annotation { "Feature Type Name" : "Feature", "Feature Type Description" : "" }
export const myFeature = defineFeature(function(context is Context, id is Id, definition is map)
    precondition{}
    {
        {
            var Q0;
            Q0=qCreatedBy(makeId("Front.planeOp"),FACE);
            var sketch = newSketch(context, id + "F0", { "sketchPlane" : qUnion([Q0])});
            skLineSegment(sketch, "E0.bottom", {"start": v(-339.73, -6.1) * mm, "end": v(339.73, -6.1) * mm});
            skLineSegment(sketch, "E0.top", {"start": v(-339.73, -31.5) * mm, "end": v(339.73, -31.5) * mm});
            skLineSegment(sketch, "E0.left", {"start": v(-339.73, -6.1) * mm, "end": v(-339.73, -31.5) * mm});
            skLineSegment(sketch, "E0.right", {"start": v(339.73, -6.1) * mm, "end": v(339.73, -31.5) * mm});
            skPoint(sketch, "E1", {"position": v(0, -6.1) * mm});
            skPoint(sketch, "E2", {"position": v(0, -31.5) * mm});
            skSolve(sketch);
        }
        {
            var Q0;
            Q0=makeQuery(id+"F0.imprint","IMPRINT",FACE,{"disambiguationData":[TD([[makeQuery(id+"F0.imprint","IMPRINT",EDGE,{"derivedFrom":sQuery(id+"F0.wireOp",EDGE,"E0.bottom")}),-1.0]])]});
            extrude(context, id + "F1", {"entities" : qUnion([Q0]), "depth" : 12.7 * mm, "offsetDistance" : 25.4 * mm});
        }
        {
            var Q0;
            Q0=makeQuery(id+"Fdx1QHjnCxCHuVW_1.boolean.opBoolean","MERGE",FACE,{"derivedFrom":[makeQuery(id+"F1.opExtrude","CAP_FACE",FACE,{"disambiguationData":[OSD([sQuery(id+"F0.wireOp",EDGE,"E0.bottom"),sQuery(id+"F0.wireOp",EDGE,"E0.top"),sQuery(id+"F0.wireOp",EDGE,"E0.left"),sQuery(id+"F0.wireOp",EDGE,"E0.right")])],"isStart":false}),makeQuery(id+"Fdx1QHjnCxCHuVW_1.opExtrude","CAP_FACE",FACE,{"disambiguationData":[OSD([sQuery(id+"FkjEasT6BlErXXm_1.wireOp",EDGE,"e268084d-6bfb-4e87-9f2a-011bc5352065.sketch_text.stroke-0"),sQuery(id+"FkjEasT6BlErXXm_1.wireOp",EDGE,"e268084d-6bfb-4e87-9f2a-011bc5352065.sketch_text.stroke-1"),sQuery(id+"FkjEasT6BlErXXm_1.wireOp",EDGE,"e268084d-6bfb-4e87-9f2a-011bc5352065.sketch_text.stroke-2"),sQuery(id+"FkjEasT6BlErXXm_1.wireOp",EDGE,"e268084d-6bfb-4e87-9f2a-011bc5352065.sketch_text.stroke-3")])],"isStart":true}),makeQuery(id+"Fdx1QHjnCxCHuVW_1.opExtrude","CAP_FACE",FACE,{"disambiguationData":[OSD([sQuery(id+"FkjEasT6BlErXXm_1.wireOp",EDGE,"e268084d-6bfb-4e87-9f2a-011bc5352065.sketch_text.stroke-4"),sQuery(id+"FkjEasT6BlErXXm_1.wireOp",EDGE,"e268084d-6bfb-4e87-9f2a-011bc5352065.sketch_text.stroke-5"),sQuery(id+"FkjEasT6BlErXXm_1.wireOp",EDGE,"e268084d-6bfb-4e87-9f2a-011bc5352065.sketch_text.stroke-6"),sQuery(id+"FkjEasT6BlErXXm_1.wireOp",EDGE,"e268084d-6bfb-4e87-9f2a-011bc5352065.sketch_text.stroke-7"),sQuery(id+"FkjEasT6BlErXXm_1.wireOp",EDGE,"e268084d-6bfb-4e87-9f2a-011bc5352065.sketch_text.stroke-8"),sQuery(id+"FkjEasT6BlErXXm_1.wireOp",EDGE,"e268084d-6bfb-4e87-9f2a-011bc5352065.sketch_text.stroke-9"),sQuery(id+"FkjEasT6BlErXXm_1.wireOp",EDGE,"e268084d-6bfb-4e87-9f2a-011bc5352065.sketch_text.stroke-10"),sQuery(id+"FkjEasT6BlErXXm_1.wireOp",EDGE,"e268084d-6bfb-4e87-9f2a-011bc5352065.sketch_text.stroke-11"),sQuery(id+"FkjEasT6BlErXXm_1.wireOp",EDGE,"e268084d-6bfb-4e87-9f2a-011bc5352065.sketch_text.stroke-12"),sQuery(id+"FkjEasT6BlErXXm_1.wireOp",EDGE,"e268084d-6bfb-4e87-9f2a-011bc5352065.sketch_text.stroke-13"),sQuery(id+"FkjEasT6BlErXXm_1.wireOp",EDGE,"e268084d-6bfb-4e87-9f2a-011bc5352065.sketch_text.stroke-14"),sQuery(id+"FkjEasT6BlErXXm_1.wireOp",EDGE,"e268084d-6bfb-4e87-9f2a-011bc5352065.sketch_text.stroke-15"),sQuery(id+"FkjEasT6BlErXXm_1.wireOp",EDGE,"e268084d-6bfb-4e87-9f2a-011bc5352065.sketch_text.stroke-16"),sQuery(id+"FkjEasT6BlErXXm_1.wireOp",EDGE,"e268084d-6bfb-4e87-9f2a-011bc5352065.sketch_text.stroke-17"),sQuery(id+"FkjEasT6BlErXXm_1.wireOp",EDGE,"e268084d-6bfb-4e87-9f2a-011bc5352065.sketch_text.stroke-18"),sQuery(id+"FkjEasT6BlErXXm_1.wireOp",EDGE,"e268084d-6bfb-4e87-9f2a-011bc5352065.sketch_text.stroke-19"),sQuery(id+"FkjEasT6BlErXXm_1.wireOp",EDGE,"e268084d-6bfb-4e87-9f2a-011bc5352065.sketch_text.stroke-20"),sQuery(id+"FkjEasT6BlErXXm_1.wireOp",EDGE,"e268084d-6bfb-4e87-9f2a-011bc5352065.sketch_text.stroke-21"),sQuery(id+"FkjEasT6BlErXXm_1.wireOp",EDGE,"e268084d-6bfb-4e87-9f2a-011bc5352065.sketch_text.stroke-22"),sQuery(id+"FkjEasT6BlErXXm_1.wireOp",EDGE,"e268084d-6bfb-4e87-9f2a-011bc5352065.sketch_text.stroke-23"),sQuery(id+"FkjEasT6BlErXXm_1.wireOp",EDGE,"e268084d-6bfb-4e87-9f2a-011bc5352065.sketch_text.stroke-24"),sQuery(id+"FkjEasT6BlErXXm_1.wireOp",EDGE,"e268084d-6bfb-4e87-9f2a-011bc5352065.sketch_text.stroke-25"),sQuery(id+"FkjEasT6BlErXXm_1.wireOp",EDGE,"e268084d-6bfb-4e87-9f2a-011bc5352065.sketch_text.stroke-26"),sQuery(id+"FkjEasT6BlErXXm_1.wireOp",EDGE,"e268084d-6bfb-4e87-9f2a-011bc5352065.sketch_text.stroke-27"),sQuery(id+"FkjEasT6BlErXXm_1.wireOp",EDGE,"e268084d-6bfb-4e87-9f2a-011bc5352065.sketch_text.stroke-28"),sQuery(id+"FkjEasT6BlErXXm_1.wireOp",EDGE,"e268084d-6bfb-4e87-9f2a-011bc5352065.sketch_text.stroke-29"),sQuery(id+"FkjEasT6BlErXXm_1.wireOp",EDGE,"e268084d-6bfb-4e87-9f2a-011bc5352065.sketch_text.stroke-30"),sQuery(id+"FkjEasT6BlErXXm_1.wireOp",EDGE,"e268084d-6bfb-4e87-9f2a-011bc5352065.sketch_text.stroke-31")])],"isStart":true}),makeQuery(id+"Fdx1QHjnCxCHuVW_1.opExtrude","CAP_FACE",FACE,{"disambiguationData":[OSD([sQuery(id+"FkjEasT6BlErXXm_1.wireOp",EDGE,"e268084d-6bfb-4e87-9f2a-011bc5352065.sketch_text.stroke-32"),sQuery(id+"FkjEasT6BlErXXm_1.wireOp",EDGE,"e268084d-6bfb-4e87-9f2a-011bc5352065.sketch_text.stroke-33"),sQuery(id+"FkjEasT6BlErXXm_1.wireOp",EDGE,"e268084d-6bfb-4e87-9f2a-011bc5352065.sketch_text.stroke-34"),sQuery(id+"FkjEasT6BlErXXm_1.wireOp",EDGE,"e268084d-6bfb-4e87-9f2a-011bc5352065.sketch_text.stroke-35"),sQuery(id+"FkjEasT6BlErXXm_1.wireOp",EDGE,"e268084d-6bfb-4e87-9f2a-011bc5352065.sketch_text.stroke-36"),sQuery(id+"FkjEasT6BlErXXm_1.wireOp",EDGE,"e268084d-6bfb-4e87-9f2a-011bc5352065.sketch_text.stroke-37"),sQuery(id+"FkjEasT6BlErXXm_1.wireOp",EDGE,"e268084d-6bfb-4e87-9f2a-011bc5352065.sketch_text.stroke-38"),sQuery(id+"FkjEasT6BlErXXm_1.wireOp",EDGE,"e268084d-6bfb-4e87-9f2a-011bc5352065.sketch_text.stroke-39"),sQuery(id+"FkjEasT6BlErXXm_1.wireOp",EDGE,"e268084d-6bfb-4e87-9f2a-011bc5352065.sketch_text.stroke-40"),sQuery(id+"FkjEasT6BlErXXm_1.wireOp",EDGE,"e268084d-6bfb-4e87-9f2a-011bc5352065.sketch_text.stroke-41"),sQuery(id+"FkjEasT6BlErXXm_1.wireOp",EDGE,"e268084d-6bfb-4e87-9f2a-011bc5352065.sketch_text.stroke-42"),sQuery(id+"FkjEasT6BlErXXm_1.wireOp",EDGE,"e268084d-6bfb-4e87-9f2a-011bc5352065.sketch_text.stroke-43")])],"isStart":true}),makeQuery(id+"Fdx1QHjnCxCHuVW_1.opExtrude","CAP_FACE",FACE,{"disambiguationData":[OSD([sQuery(id+"FkjEasT6BlErXXm_1.wireOp",EDGE,"e268084d-6bfb-4e87-9f2a-011bc5352065.sketch_text.stroke-44"),sQuery(id+"FkjEasT6BlErXXm_1.wireOp",EDGE,"e268084d-6bfb-4e87-9f2a-011bc5352065.sketch_text.stroke-45"),sQuery(id+"FkjEasT6BlErXXm_1.wireOp",EDGE,"e268084d-6bfb-4e87-9f2a-011bc5352065.sketch_text.stroke-46"),sQuery(id+"FkjEasT6BlErXXm_1.wireOp",EDGE,"e268084d-6bfb-4e87-9f2a-011bc5352065.sketch_text.stroke-47")])],"isStart":true}),makeQuery(id+"Fdx1QHjnCxCHuVW_1.opExtrude","CAP_FACE",FACE,{"disambiguationData":[OSD([sQuery(id+"FkjEasT6BlErXXm_1.wireOp",EDGE,"e268084d-6bfb-4e87-9f2a-011bc5352065.sketch_text.stroke-48"),sQuery(id+"FkjEasT6BlErXXm_1.wireOp",EDGE,"e268084d-6bfb-4e87-9f2a-011bc5352065.sketch_text.stroke-49"),sQuery(id+"FkjEasT6BlErXXm_1.wireOp",EDGE,"e268084d-6bfb-4e87-9f2a-011bc5352065.sketch_text.stroke-50"),sQuery(id+"FkjEasT6BlErXXm_1.wireOp",EDGE,"e268084d-6bfb-4e87-9f2a-011bc5352065.sketch_text.stroke-51"),sQuery(id+"FkjEasT6BlErXXm_1.wireOp",EDGE,"e268084d-6bfb-4e87-9f2a-011bc5352065.sketch_text.stroke-52"),sQuery(id+"FkjEasT6BlErXXm_1.wireOp",EDGE,"e268084d-6bfb-4e87-9f2a-011bc5352065.sketch_text.stroke-53"),sQuery(id+"FkjEasT6BlErXXm_1.wireOp",EDGE,"e268084d-6bfb-4e87-9f2a-011bc5352065.sketch_text.stroke-54"),sQuery(id+"FkjEasT6BlErXXm_1.wireOp",EDGE,"e268084d-6bfb-4e87-9f2a-011bc5352065.sketch_text.stroke-55"),sQuery(id+"FkjEasT6BlErXXm_1.wireOp",EDGE,"e268084d-6bfb-4e87-9f2a-011bc5352065.sketch_text.stroke-56"),sQuery(id+"FkjEasT6BlErXXm_1.wireOp",EDGE,"e268084d-6bfb-4e87-9f2a-011bc5352065.sketch_text.stroke-57"),sQuery(id+"FkjEasT6BlErXXm_1.wireOp",EDGE,"e268084d-6bfb-4e87-9f2a-011bc5352065.sketch_text.stroke-58"),sQuery(id+"FkjEasT6BlErXXm_1.wireOp",EDGE,"e268084d-6bfb-4e87-9f2a-011bc5352065.sketch_text.stroke-59")])],"isStart":true}),makeQuery(id+"Fdx1QHjnCxCHuVW_1.opExtrude","CAP_FACE",FACE,{"disambiguationData":[OSD([sQuery(id+"FkjEasT6BlErXXm_1.wireOp",EDGE,"e268084d-6bfb-4e87-9f2a-011bc5352065.sketch_text.stroke-60"),sQuery(id+"FkjEasT6BlErXXm_1.wireOp",EDGE,"e268084d-6bfb-4e87-9f2a-011bc5352065.sketch_text.stroke-61"),sQuery(id+"FkjEasT6BlErXXm_1.wireOp",EDGE,"e268084d-6bfb-4e87-9f2a-011bc5352065.sketch_text.stroke-62"),sQuery(id+"FkjEasT6BlErXXm_1.wireOp",EDGE,"e268084d-6bfb-4e87-9f2a-011bc5352065.sketch_text.stroke-63"),sQuery(id+"FkjEasT6BlErXXm_1.wireOp",EDGE,"e268084d-6bfb-4e87-9f2a-011bc5352065.sketch_text.stroke-64"),sQuery(id+"FkjEasT6BlErXXm_1.wireOp",EDGE,"e268084d-6bfb-4e87-9f2a-011bc5352065.sketch_text.stroke-65"),sQuery(id+"FkjEasT6BlErXXm_1.wireOp",EDGE,"e268084d-6bfb-4e87-9f2a-011bc5352065.sketch_text.stroke-66"),sQuery(id+"FkjEasT6BlErXXm_1.wireOp",EDGE,"e268084d-6bfb-4e87-9f2a-011bc5352065.sketch_text.stroke-67"),sQuery(id+"FkjEasT6BlErXXm_1.wireOp",EDGE,"e268084d-6bfb-4e87-9f2a-011bc5352065.sketch_text.stroke-68"),sQuery(id+"FkjEasT6BlErXXm_1.wireOp",EDGE,"e268084d-6bfb-4e87-9f2a-011bc5352065.sketch_text.stroke-69"),sQuery(id+"FkjEasT6BlErXXm_1.wireOp",EDGE,"e268084d-6bfb-4e87-9f2a-011bc5352065.sketch_text.stroke-70"),sQuery(id+"FkjEasT6BlErXXm_1.wireOp",EDGE,"e268084d-6bfb-4e87-9f2a-011bc5352065.sketch_text.stroke-71")])],"isStart":true})]});
            var sketch = newSketch(context, id + "F2", { "sketchPlane" : qUnion([Q0])});
            skPoint(sketch, "E3", {"position": v(-339.73, -18.8) * mm});
            skPoint(sketch, "E4", {"position": v(339.73, -18.8) * mm});
            skPoint(sketch, "E5", {"position": v(263.53, -6.1) * mm});
            skPoint(sketch, "E6", {"position": v(307.98, -6.1) * mm});
            skPoint(sketch, "E7", {"position": v(-307.98, -6.1) * mm});
            skPoint(sketch, "E8", {"position": v(-263.53, -6.1) * mm});
            skLineSegment(sketch, "E9", {"start": v(-307.98, -6.1) * mm, "end": v(-307.98, -11.18) * mm});
            skLineSegment(sketch, "E10", {"start": v(307.98, -6.1) * mm, "end": v(307.98, -11.18) * mm});
            skFitSpline(sketch, "E11", {"points": [v(-339.73, -18.8) * mm, v(-307.98, -11.18) * mm, v(-263.53, -6.1) * mm], "startDerivative": vector(65.8, 18.18) * mm, "endDerivative": vector(86.07, 7.5) * mm});
            skFitSpline(sketch, "E12", {"points": [v(263.53, -6.1) * mm, v(307.98, -11.18) * mm, v(339.73, -18.8) * mm], "startDerivative": vector(86.07, -7.5) * mm, "endDerivative": vector(65.8, -18.18) * mm});
            skSolve(sketch);
        }
        {
            var Q0;
            {var subQ0=sQuery(id+"F2.wireOp",EDGE,"E10");Q0=makeQuery(id+"F2.imprint","IMPRINT",FACE,{"disambiguationData":[TD([[makeQuery(id+"F2.imprint","IMPRINT",EDGE,{"derivedFrom":subQ0}),1.0]])]});}
            var Q1;
            {var subQ0=sQuery(id+"F2.wireOp",EDGE,"E10");Q1=makeQuery(id+"F2.imprint","IMPRINT",FACE,{"disambiguationData":[TD([[makeQuery(id+"F2.imprint","IMPRINT",EDGE,{"derivedFrom":subQ0}),-1.0]])]});}
            var Q2;
            {var subQ0=sQuery(id+"F2.wireOp",EDGE,"E9");Q2=makeQuery(id+"F2.imprint","IMPRINT",FACE,{"disambiguationData":[TD([[makeQuery(id+"F2.imprint","IMPRINT",EDGE,{"derivedFrom":subQ0}),-1.0]])]});}
            var Q3;
            {var subQ0=sQuery(id+"F2.wireOp",EDGE,"E9");Q3=makeQuery(id+"F2.imprint","IMPRINT",FACE,{"disambiguationData":[TD([[makeQuery(id+"F2.imprint","IMPRINT",EDGE,{"derivedFrom":subQ0}),1.0]])]});}
            extrude(context, id + "F3", {"entities" : qUnion([Q0, Q1, Q2, Q3]), "operationType" : NewBodyOperationType.REMOVE, "oppositeDirection" : true, "depth" : 12.7 * mm, "offsetDistance" : 25.4 * mm});
        }
        {
            var Q0;
            Q0=makeQuery(id+"F1.opExtrude","CAP_FACE",FACE,{"disambiguationData":[OSD([sQuery(id+"F0.wireOp",EDGE,"E0.bottom"),sQuery(id+"F0.wireOp",EDGE,"E0.top"),sQuery(id+"F0.wireOp",EDGE,"E0.left"),sQuery(id+"F0.wireOp",EDGE,"E0.right")])],"isStart":false});
            var sketch = newSketch(context, id + "F4", { "sketchPlane" : qUnion([Q0])});
            skText(sketch, "E13", { "text": "SAMARA RESNICK", "fontName": "OpenSans-Bold.ttf"});
            const initialGuessF4  = {"E13": [-0.26211, -0.0061, 1, 0, 0.04268]};
            skSetInitialGuess(sketch, initialGuessF4);
            skSolve(sketch);
        }
        {
            var Q0;
            Q0 = qSketchRegion(id + "F4", true);
            extrude(context, id + "F5", {"entities" : qUnion([Q0]), "operationType" : NewBodyOperationType.ADD, "depth" : -12.7 * mm, "offsetDistance" : 25.4 * mm});
        }
    });